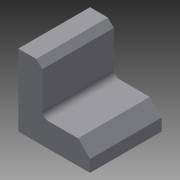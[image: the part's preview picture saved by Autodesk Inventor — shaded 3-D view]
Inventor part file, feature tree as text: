
AUTODESK INVENTOR PART (.ipt)
format: ipt  version: 2015 (Build 190159000, 159)  size: 93,696 bytes
history: native  units: in
note: dims shown in document units (in); Inventor stores cm internally (conversion verified against a paired STEP export)
features: extrude x2, chamfer x2, sketch x2, fillet x1
ambient origin geometry x8: Origin, YZ Plane, XZ Plane, XY Plane, X Axis, Y Axis, Z Axis, Center Point
bodies: Solid1 (feature_tree)
feature tree (7):
  extrude  "Extrusion1"  Depth=1.5in
  extrude  "Extrusion2"  Depth=0.5in
  fillet  "Fillet4"  [1 undecoded]
  chamfer  "Chamfer5"  Distance=0.125in
  chamfer  "Chamfer6"  Distance=0.125in Angle=45.0deg
  sketch  "Sketch1"  dims[d0=1.5in d1=1.5in]
  sketch  "Sketch2"  dims[d2=1.5in d3=0.0in d5=0.5in d8=0.0in d9=0.0in d25=0.125in d26=0.125in d27=0.125in d28=45.0deg d29=0.25in d30=0.125in d31=45.0deg]
note: 1 required parameter value undecoded (feature->parameter linkage not recoverable at this tier; creation-order binding heuristic only, values carry confidence <= 0.55)
